# Revit family: 11 OVERTIME
name_source: partatom
category: Arredi
units: mm (PartAtom-declared; Revit-internal decimal feet)

## family parameters
Basato su piano di lavoro = Sì
Condiviso = No
Punto di calcolo locali = No
Sempre verticale = Sì
Taglio con vuoti quando caricato = No

## types (23) — shared parameters
Imbottiture = 3518_Luxy_Imbottiture
Prospetto di default = 1219 mm
Struttura = 3518_Luxy_Struttura

## per-type parameters (varying)
| type | Bracciolo 1D | Bracciolo 3D | Gambe Fisse | Mec_Syncron | Poggiatesta | Ruote 50 | Ruote 65 | Soluzione |
| 2200_4OVDI20 | No | Sì | No | Sì | Sì | No | Sì | 3 |
| 2200_4OVDI26 | No | Sì | No | Sì | Sì | Sì | No | 2 |
| 2210R_4OVGI70 | No | Sì | No | Sì | No | No | Sì | 3 |
| 2210R_4OVGI76 | No | Sì | No | Sì | No | Sì | No | 2 |
| 2210R_4OVGI76099NE | No | Sì | No | Sì | No | Sì | No | 2 |
| 2210D_4OVGI78 | Sì | No | No | Sì | No | No | Sì | 3 |
| 2210D_4OVGI84 | Sì | No | No | Sì | No | Sì | No | 2 |
| 2210_4OVGI86 | No | No | No | Sì | No | No | Sì | 3 |
| 2210_4OVGI92 | No | No | No | Sì | No | Sì | No | 2 |
| 2400_4OVDI28 | No | Sì | No | Sì | Sì | No | Sì | 3 |
| 2400_4OVDI34 | No | Sì | No | Sì | Sì | Sì | No | 2 |
| 2410R_4OVGI94 | No | Sì | No | Sì | No | No | Sì | 3 |
| 2410R_4OVGI100 | No | Sì | No | Sì | No | Sì | No | 2 |
| 2410D_4OVGI102 | No | Sì | No | Sì | No | No | Sì | 3 |
| 2410D_4OVGI108 | No | Sì | No | Sì | No | Sì | No | 2 |
| 2410_4OVGI110 | No | No | No | Sì | No | No | Sì | 3 |
| 2410_4OVGI116 | No | No | No | Sì | No | Sì | No | 2 |
| 2900R_4OVFI18 | No | Sì | Sì | No | No | No | No | 1 |
| 2900R_4OVFI24 | No | Sì | Sì | No | No | No | No | 1 |
| 2900D_4OVFI42 | Sì | No | Sì | No | No | No | No | 1 |
| 2900D_4OVFI48 | Sì | No | Sì | No | No | No | No | 1 |
| 2900_4OVFI34 | No | No | Sì | No | No | No | No | 1 |
| 2900_4OVFI40 | No | No | Sì | No | No | No | No | 1 |

## geometry (parser evidence)
native form markers: Sweep x3
no freeform markers — native parametric forms only
